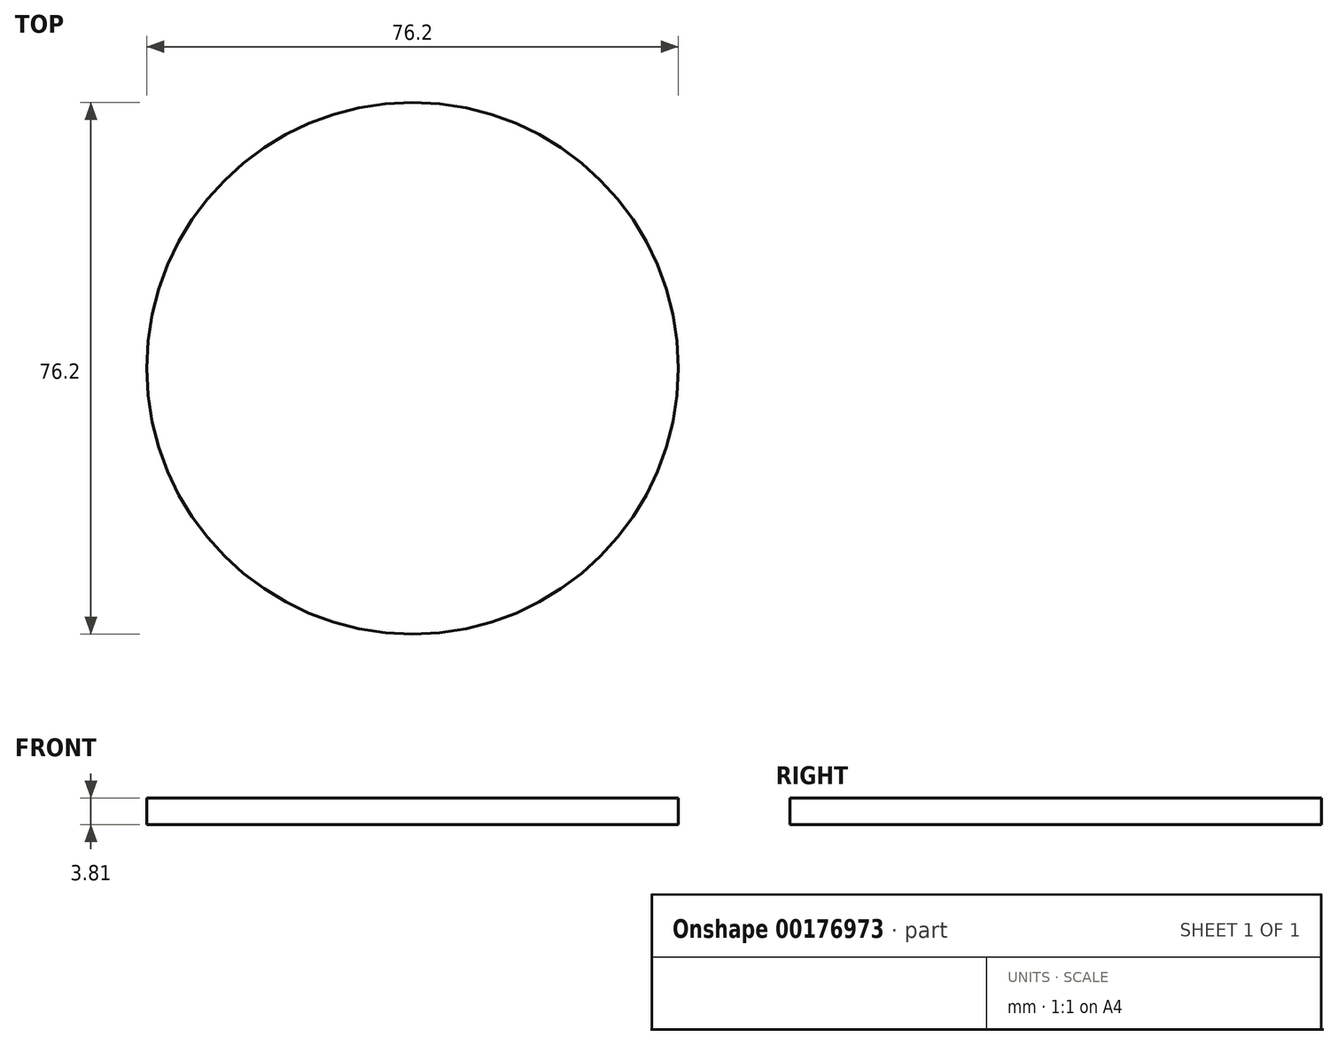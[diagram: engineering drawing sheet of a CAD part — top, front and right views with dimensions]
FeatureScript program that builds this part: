
annotation { "Feature Type Name" : "Feature", "Feature Type Description" : "" }
export const myFeature = defineFeature(function(context is Context, id is Id, definition is map)
    precondition{}
    {
        {
            var Q0;
            Q0=qCreatedBy(makeId("Top.planeOp"),FACE);
            var sketch = newSketch(context, id + "F0", { "sketchPlane" : qUnion([Q0])});
            skCircle(sketch, "E0", {"center": v(0, 0) * mm, "radius": 38.1 * mm});
            skSolve(sketch);
        }
        {
            var Q0;
            Q0=makeQuery(id+"F0.imprint","IMPRINT",FACE,{"disambiguationData":[TD([[makeQuery(id+"F0.imprint","IMPRINT",EDGE,{"derivedFrom":sQuery(id+"F0.wireOp",EDGE,"E0")}),1.0]])]});
            var Q1;
            Q1 = qSketchRegion(id + "F2", true);
            extrude(context, id + "F1", {"entities" : qUnion([Q0, Q1]), "depth" : 3.8 * mm});
        }
    });
